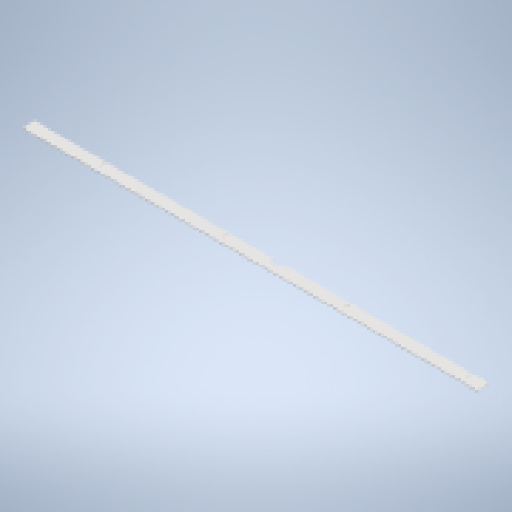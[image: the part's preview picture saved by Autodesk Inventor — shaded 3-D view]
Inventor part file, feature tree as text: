
AUTODESK INVENTOR PART (.ipt)
format: ipt  version: 2025 (Build 290162010, 162A)  size: 322,560 bytes
history: native  units: mm
features: sketch x4, other x3, extrude x2, sheet_metal_op x1, pattern_linear x1, projected_geometry x1
ambient origin geometry x8: Origin, YZ Plane, XZ Plane, XY Plane, X Axis, Y Axis, Z Axis, Center Point
bodies: Body1 (feature_tree)
feature tree (12):
  sheet_metal_op  "Face3"
  extrude  "Extrusion3"  Depth=1860.0mm
  pattern_linear  "Rectangular Pattern2"  Spacing1=26.0mm  [1 undecoded]
  extrude  "Extrusion4"  TaperAngle=0.0deg  [1 undecoded]
  other  "Mark1"
  sketch  "Sketch8"  dims[d37=50.0mm d38=1860.0mm]
  other  "Plate5"
  sketch  "Sketch9"  dims[d41=3.0mm]
  sketch  "Sketch10"  dims[d42=146.0mm]
  projected_geometry  "Projected Loop2"
  sketch  "Sketch11"  dims[d43=3.2mm d44=26.0mm d45=0.0mm d46=0.0mm d47=60.0mm d49=500.0mm d50=40.0mm d52=1370.0mm d53=0.0mm d54=0.0mm]
  other  "Definition1"
note: 2 required parameter values undecoded (feature->parameter linkage not recoverable at this tier; creation-order binding heuristic only, values carry confidence <= 0.55)
